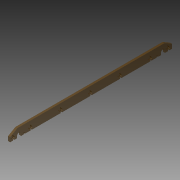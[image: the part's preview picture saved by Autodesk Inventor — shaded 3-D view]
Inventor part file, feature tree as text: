
AUTODESK INVENTOR PART (.ipt)
format: ipt  version: 2014 SP1 (Build 180222100, 222)  size: 228,352 bytes
history: native  units: mm
features: extrude x1, sketch x1
ambient origin geometry x8: Origin, YZ Plane, XZ Plane, XY Plane, X Axis, Y Axis, Z Axis, Center Point
bodies: Solid1 (feature_tree)
feature tree (2):
  extrude  "Extrusion1"  Depth=20.0mm
  sketch  "Sketch1"  dims[d0=375.62919mm d1=20.0mm d2=10.185045mm d3=17.0mm d4=341.613851mm d5=20.81536mm d6=334.013809mm d7=4.7625mm d8=0.0mm]
